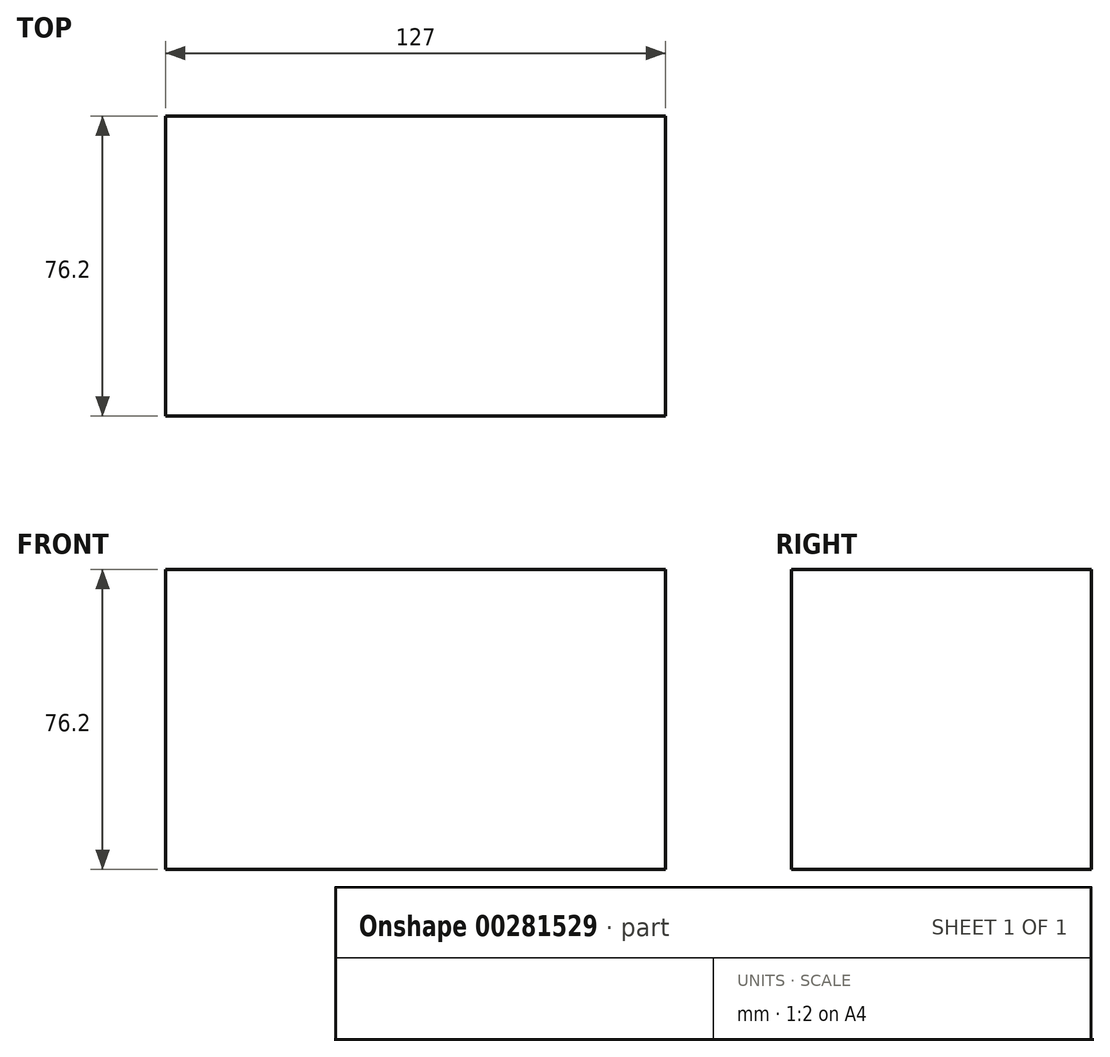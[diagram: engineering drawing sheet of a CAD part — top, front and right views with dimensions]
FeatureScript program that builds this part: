
annotation { "Feature Type Name" : "Feature", "Feature Type Description" : "" }
export const myFeature = defineFeature(function(context is Context, id is Id, definition is map)
    precondition{}
    {
        {
            var Q0;
            Q0=qCreatedBy(makeId("Front.planeOp"),FACE);
            var sketch = newSketch(context, id + "F0", { "sketchPlane" : qUnion([Q0])});
            skLineSegment(sketch, "E0.bottom", {"start": v(-75, 34.65) * mm, "end": v(52, 34.65) * mm});
            skLineSegment(sketch, "E0.top", {"start": v(-75, -41.55) * mm, "end": v(52, -41.55) * mm});
            skLineSegment(sketch, "E0.left", {"start": v(-75, 34.65) * mm, "end": v(-75, -41.55) * mm});
            skLineSegment(sketch, "E0.right", {"start": v(52, 34.65) * mm, "end": v(52, -41.55) * mm});
            skSolve(sketch);
        }
        {
            var Q0;
            Q0 = qSketchRegion(id + "F0", true);
            extrude(context, id + "F1", {"entities" : qUnion([Q0]), "depth" : 76.2 * mm});
        }
    });
